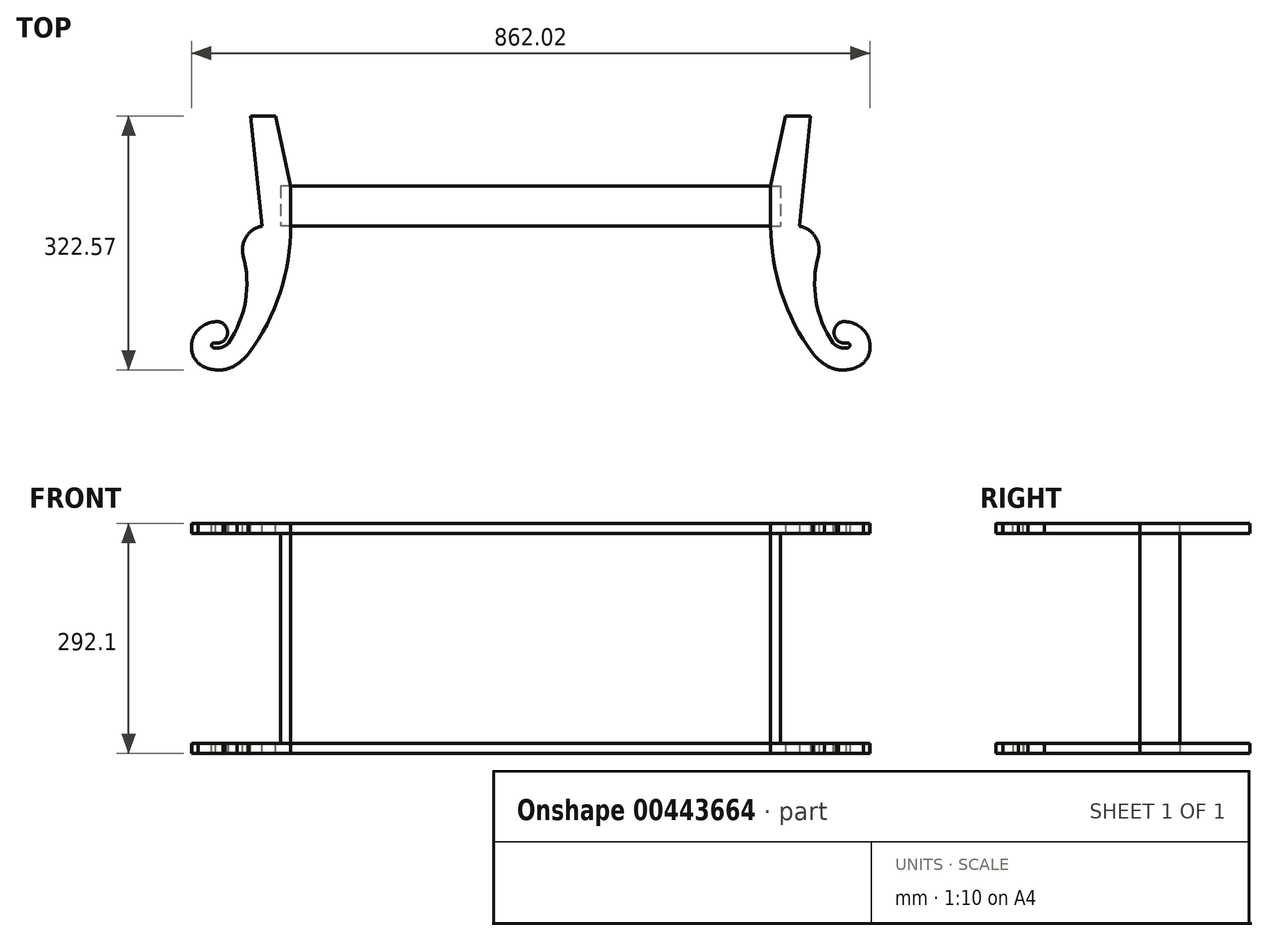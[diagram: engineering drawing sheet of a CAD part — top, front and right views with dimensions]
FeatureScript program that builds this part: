
annotation { "Feature Type Name" : "Feature", "Feature Type Description" : "" }
export const myFeature = defineFeature(function(context is Context, id is Id, definition is map)
    precondition{}
    {
        {
            var Q0;
            Q0=qCreatedBy(makeId("Front.planeOp"),FACE);
            var sketch = newSketch(context, id + "F0", { "sketchPlane" : qUnion([Q0])});
            skLineSegment(sketch, "E0.bottom", {"start": v(0, 0) * mm, "end": v(-609.6, 0) * mm});
            skLineSegment(sketch, "E0.top", {"start": v(0, 266.7) * mm, "end": v(-609.6, 266.7) * mm});
            skLineSegment(sketch, "E0.left", {"start": v(0, 0) * mm, "end": v(0, 266.7) * mm});
            skLineSegment(sketch, "E0.right", {"start": v(-609.6, 0) * mm, "end": v(-609.6, 266.7) * mm});
            skLineSegment(sketch, "E1.0", {"start": v(0, 279.4) * mm, "end": v(-609.6, 279.4) * mm});
            skLineSegment(sketch, "E1.1", {"start": v(12.7, 0) * mm, "end": v(12.7, 266.7) * mm});
            skLineSegment(sketch, "E1.2", {"start": v(0, -12.7) * mm, "end": v(-609.6, -12.7) * mm});
            skLineSegment(sketch, "E1.3", {"start": v(-622.3, 0) * mm, "end": v(-622.3, 266.7) * mm});
            skLineSegment(sketch, "E2", {"start": v(0, 266.7) * mm, "end": v(0, 279.4) * mm});
            skLineSegment(sketch, "E3", {"start": v(0, 266.7) * mm, "end": v(12.7, 266.7) * mm});
            skLineSegment(sketch, "E4", {"start": v(-609.6, 266.7) * mm, "end": v(-609.6, 279.4) * mm});
            skLineSegment(sketch, "E5", {"start": v(-609.6, 266.7) * mm, "end": v(-622.3, 266.7) * mm});
            skLineSegment(sketch, "E6", {"start": v(-609.6, 0) * mm, "end": v(-609.6, -12.7) * mm});
            skLineSegment(sketch, "E7", {"start": v(-609.6, 0) * mm, "end": v(-622.3, 0) * mm});
            skLineSegment(sketch, "E8", {"start": v(0, 0) * mm, "end": v(0, -12.7) * mm});
            skLineSegment(sketch, "E9", {"start": v(0, 0) * mm, "end": v(12.7, 0) * mm});
            skSolve(sketch);
        }
        {
            var Q0;
            Q0=makeQuery(id+"F0.imprint","IMPRINT",FACE,{"disambiguationData":[TD([[makeQuery(id+"F0.imprint","IMPRINT",EDGE,{"derivedFrom":sQuery(id+"F0.wireOp",EDGE,"E0.top")}),-1.0]])]});
            var Q1;
            Q1=makeQuery(id+"F0.imprint","IMPRINT",FACE,{"disambiguationData":[TD([[makeQuery(id+"F0.imprint","IMPRINT",EDGE,{"derivedFrom":sQuery(id+"F0.wireOp",EDGE,"E0.right")}),1.0]])]});
            var Q2;
            Q2=makeQuery(id+"F0.imprint","IMPRINT",FACE,{"disambiguationData":[TD([[makeQuery(id+"F0.imprint","IMPRINT",EDGE,{"derivedFrom":sQuery(id+"F0.wireOp",EDGE,"E0.bottom")}),1.0]])]});
            var Q3;
            Q3=makeQuery(id+"F0.imprint","IMPRINT",FACE,{"disambiguationData":[TD([[makeQuery(id+"F0.imprint","IMPRINT",EDGE,{"derivedFrom":sQuery(id+"F0.wireOp",EDGE,"E0.left")}),-1.0]])]});
            extrude(context, id + "F1", {"entities" : qUnion([Q0, Q1, Q2, Q3]), "oppositeDirection" : true, "depth" : 50.8 * mm});
        }
        {
            var Q0;
            Q0=makeQuery(id+"F1.opExtrude","SWEPT_FACE",FACE,{"disambiguationData":[OSD([sQuery(id+"F0.wireOp",EDGE,"E7")])]});
            var sketch = newSketch(context, id + "F2", { "sketchPlane" : qUnion([Q0])});
            skLineSegment(sketch, "E10", {"start": v(-660.4, -139.7) * mm, "end": v(-628.65, -139.7) * mm});
            skLineSegment(sketch, "E11", {"start": v(-609.6, -50.8) * mm, "end": v(-609.6, 0) * mm});
            skArc(sketch, "E12", {"start": v(-705.02, 121.4) * mm, "mid": v(-689.95, 135.71) * mm, "end": v(-706.36, 148.46) * mm});
            skArc(sketch, "E13", {"start": v(-688.65, 148.37) * mm, "mid": v(-697.3, 154.06) * mm, "end": v(-707.63, 154.68) * mm});
            skArc(sketch, "E14", {"start": v(-707.63, 154.68) * mm, "mid": v(-710.1, 150.94) * mm, "end": v(-706.36, 148.46) * mm});
            skArc(sketch, "E15", {"start": v(-609.6, 0) * mm, "mid": v(-623.28, 85.15) * mm, "end": v(-662.94, 161.73) * mm});
            skArc(sketch, "E16", {"start": v(-735.81, 154.3) * mm, "mid": v(-735.37, 148.14) * mm, "end": v(-733.92, 142.12) * mm});
            skPoint(sketch, "E17.start.orphan", {"position": v(-706.36, 182.77) * mm});
            skArc(sketch, "E18.trimOffspring", {"start": v(-733.92, 142.12) * mm, "mid": v(-722.3, 127.82) * mm, "end": v(-705.02, 121.4) * mm});
            skArc(sketch, "E19", {"start": v(-693.54, 182.23) * mm, "mid": v(-694.66, 182.44) * mm, "end": v(-695.78, 182.63) * mm});
            skArc(sketch, "E20", {"start": v(-695.78, 182.63) * mm, "mid": v(-704.55, 182.73) * mm, "end": v(-713.21, 181.36) * mm});
            skArc(sketch, "E21", {"start": v(-713.21, 181.36) * mm, "mid": v(-720.7, 178.48) * mm, "end": v(-727.26, 173.88) * mm});
            skArc(sketch, "E22", {"start": v(-727.26, 173.88) * mm, "mid": v(-733.45, 164.93) * mm, "end": v(-735.81, 154.3) * mm});
            skPoint(sketch, "E23.orphan", {"position": v(-691.05, 182.63) * mm});
            skArc(sketch, "E24", {"start": v(-662.94, 161.73) * mm, "mid": v(-669.92, 169.21) * mm, "end": v(-677.87, 175.63) * mm});
            skArc(sketch, "E25", {"start": v(-677.87, 175.63) * mm, "mid": v(-685.4, 179.67) * mm, "end": v(-693.54, 182.23) * mm});
            skLineSegment(sketch, "E26", {"start": v(-609.6, -50.8) * mm, "end": v(-628.65, -139.7) * mm});
            skPoint(sketch, "E27.orphan", {"position": v(-609.6, -139.7) * mm});
            skPoint(sketch, "E28.start.orphan", {"position": v(-673.1, -139.7) * mm});
            skLineSegment(sketch, "E29", {"start": v(-645.91, 0.13) * mm, "end": v(-660.4, -139.7) * mm});
            skPoint(sketch, "E30.orphan", {"position": v(-647.25, 0) * mm});
            skPoint(sketch, "E31.orphan", {"position": v(-736.6, -139.7) * mm});
            skArc(sketch, "E32", {"start": v(-670.05, 37.9) * mm, "mid": v(-666.34, 13.67) * mm, "end": v(-645.91, 0.13) * mm});
            skArc(sketch, "E33", {"start": v(-670.05, 37.9) * mm, "mid": v(-667.25, 95.17) * mm, "end": v(-688.65, 148.37) * mm});
            skSolve(sketch);
        }
        {
            var Q0;
            Q0=makeQuery(id+"F2.imprint","IMPRINT",FACE,{"disambiguationData":[TD([[makeQuery(id+"F2.imprint","IMPRINT",EDGE,{"derivedFrom":sQuery(id+"F2.wireOp",EDGE,"E10")}),1.0]])]});
            var Q1;
            Q1=makeQuery(id+"F2.imprint","IMPRINT",FACE,{"disambiguationData":[TD([[makeQuery(id+"F2.imprint","IMPRINT",EDGE,{"derivedFrom":sQuery(id+"F2.wireOp",EDGE,"E11")}),1.0]])]});
            extrude(context, id + "F3", {"entities" : qUnion([Q0, Q1]), "depth" : 12.7 * mm});
        }
        {
            var Q0;
            Q0=makeQuery(id+"F3.opExtrude","SWEPT_BODY",BODY,{"disambiguationData":[OSD([sQuery(id+"F2.wireOp",EDGE,"E10"),sQuery(id+"F2.wireOp",EDGE,"E11"),sQuery(id+"F2.wireOp",EDGE,"E12"),sQuery(id+"F2.wireOp",EDGE,"E13"),sQuery(id+"F2.wireOp",EDGE,"E14"),sQuery(id+"F2.wireOp",EDGE,"E15"),sQuery(id+"F2.wireOp",EDGE,"E16"),sQuery(id+"F2.wireOp",EDGE,"E18.trimOffspring"),sQuery(id+"F2.wireOp",EDGE,"E19"),sQuery(id+"F2.wireOp",EDGE,"E20"),sQuery(id+"F2.wireOp",EDGE,"E21"),sQuery(id+"F2.wireOp",EDGE,"E22"),sQuery(id+"F2.wireOp",EDGE,"E24"),sQuery(id+"F2.wireOp",EDGE,"E25"),sQuery(id+"F2.wireOp",EDGE,"E26"),sQuery(id+"F2.wireOp",EDGE,"E29"),sQuery(id+"F2.wireOp",EDGE,"jBR7SmMU-Rc7H-dq6u-iteg-TQdBeAZQFpAq")])]});
            transform(context, id + "F4", {"entities" : qUnion([Q0]), "transformType" : TransformType.TRANSLATION_3D, "dx" : 0 * mm, "dy" : 0 * mm, "dz" : 279.4 * mm, "makeCopy" : true});
        }
        {
            var Q0;
            Q0=makeQuery(id+"F3.opExtrude","SWEPT_BODY",BODY,{"disambiguationData":[OSD([sQuery(id+"F2.wireOp",EDGE,"E10"),sQuery(id+"F2.wireOp",EDGE,"E11"),sQuery(id+"F2.wireOp",EDGE,"E12"),sQuery(id+"F2.wireOp",EDGE,"E13"),sQuery(id+"F2.wireOp",EDGE,"E14"),sQuery(id+"F2.wireOp",EDGE,"E15"),sQuery(id+"F2.wireOp",EDGE,"E16"),sQuery(id+"F2.wireOp",EDGE,"E18.trimOffspring"),sQuery(id+"F2.wireOp",EDGE,"E19"),sQuery(id+"F2.wireOp",EDGE,"E20"),sQuery(id+"F2.wireOp",EDGE,"E21"),sQuery(id+"F2.wireOp",EDGE,"E22"),sQuery(id+"F2.wireOp",EDGE,"E24"),sQuery(id+"F2.wireOp",EDGE,"E25"),sQuery(id+"F2.wireOp",EDGE,"E26"),sQuery(id+"F2.wireOp",EDGE,"E29"),sQuery(id+"F2.wireOp",EDGE,"E32"),sQuery(id+"F2.wireOp",EDGE,"E33")])]});
            var Q1;
            Q1=makeQuery(id+"F1.opExtrude","SWEPT_EDGE",EDGE,{"disambiguationData":[OSD([sQuery(id+"F0.wireOp",EDGE,"E1.2"),sQuery(id+"F0.wireOp",EDGE,"E6")])]});
            transform(context, id + "F5", {"entities" : qUnion([Q0]), "transformType" : TransformType.ROTATION, "transformAxis" : qUnion([Q1]), "angle" : 180 * degree, "oppositeDirection" : true, "makeCopy" : true});
        }
        {
            var Q0;
            Q0=makeQuery(id+"F5.opPattern","COPY",BODY,{"derivedFrom":makeQuery(id+"F3.opExtrude","SWEPT_BODY",BODY,{"disambiguationData":[OSD([sQuery(id+"F2.wireOp",EDGE,"E10"),sQuery(id+"F2.wireOp",EDGE,"E11"),sQuery(id+"F2.wireOp",EDGE,"E12"),sQuery(id+"F2.wireOp",EDGE,"E13"),sQuery(id+"F2.wireOp",EDGE,"E14"),sQuery(id+"F2.wireOp",EDGE,"E15"),sQuery(id+"F2.wireOp",EDGE,"E16"),sQuery(id+"F2.wireOp",EDGE,"E18.trimOffspring"),sQuery(id+"F2.wireOp",EDGE,"E19"),sQuery(id+"F2.wireOp",EDGE,"E20"),sQuery(id+"F2.wireOp",EDGE,"E21"),sQuery(id+"F2.wireOp",EDGE,"E22"),sQuery(id+"F2.wireOp",EDGE,"E24"),sQuery(id+"F2.wireOp",EDGE,"E25"),sQuery(id+"F2.wireOp",EDGE,"E26"),sQuery(id+"F2.wireOp",EDGE,"E29"),sQuery(id+"F2.wireOp",EDGE,"E32"),sQuery(id+"F2.wireOp",EDGE,"E33")])]}),"instanceName":"1"});
            transform(context, id + "F6", {"entities" : qUnion([Q0]), "transformType" : TransformType.TRANSLATION_3D, "dx" : 609.6 * mm, "dy" : 0 * mm, "dz" : 12.7 * mm, "makeCopy" : true});
        }
        {
            var Q0;
            Q0=makeQuery(id+"F6.opPattern","COPY",BODY,{"derivedFrom":makeQuery(id+"F5.opPattern","COPY",BODY,{"derivedFrom":makeQuery(id+"F3.opExtrude","SWEPT_BODY",BODY,{"disambiguationData":[OSD([sQuery(id+"F2.wireOp",EDGE,"E10"),sQuery(id+"F2.wireOp",EDGE,"E11"),sQuery(id+"F2.wireOp",EDGE,"E12"),sQuery(id+"F2.wireOp",EDGE,"E13"),sQuery(id+"F2.wireOp",EDGE,"E14"),sQuery(id+"F2.wireOp",EDGE,"E15"),sQuery(id+"F2.wireOp",EDGE,"E16"),sQuery(id+"F2.wireOp",EDGE,"E18.trimOffspring"),sQuery(id+"F2.wireOp",EDGE,"E19"),sQuery(id+"F2.wireOp",EDGE,"E20"),sQuery(id+"F2.wireOp",EDGE,"E21"),sQuery(id+"F2.wireOp",EDGE,"E22"),sQuery(id+"F2.wireOp",EDGE,"E24"),sQuery(id+"F2.wireOp",EDGE,"E25"),sQuery(id+"F2.wireOp",EDGE,"E26"),sQuery(id+"F2.wireOp",EDGE,"E29"),sQuery(id+"F2.wireOp",EDGE,"E32"),sQuery(id+"F2.wireOp",EDGE,"E33")])]}),"instanceName":"1"}),"instanceName":"1"});
            transform(context, id + "F7", {"entities" : qUnion([Q0]), "transformType" : TransformType.TRANSLATION_3D, "dx" : 0 * mm, "dy" : 0 * mm, "dz" : 279.4 * mm, "makeCopy" : true});
        }
        {
            var Q0;
            Q0=makeQuery(id+"F5.opPattern","COPY",BODY,{"derivedFrom":makeQuery(id+"F3.opExtrude","SWEPT_BODY",BODY,{"disambiguationData":[OSD([sQuery(id+"F2.wireOp",EDGE,"E10"),sQuery(id+"F2.wireOp",EDGE,"E11"),sQuery(id+"F2.wireOp",EDGE,"E12"),sQuery(id+"F2.wireOp",EDGE,"E13"),sQuery(id+"F2.wireOp",EDGE,"E14"),sQuery(id+"F2.wireOp",EDGE,"E15"),sQuery(id+"F2.wireOp",EDGE,"E16"),sQuery(id+"F2.wireOp",EDGE,"E18.trimOffspring"),sQuery(id+"F2.wireOp",EDGE,"E19"),sQuery(id+"F2.wireOp",EDGE,"E20"),sQuery(id+"F2.wireOp",EDGE,"E21"),sQuery(id+"F2.wireOp",EDGE,"E22"),sQuery(id+"F2.wireOp",EDGE,"E24"),sQuery(id+"F2.wireOp",EDGE,"E25"),sQuery(id+"F2.wireOp",EDGE,"E26"),sQuery(id+"F2.wireOp",EDGE,"E29"),sQuery(id+"F2.wireOp",EDGE,"E32"),sQuery(id+"F2.wireOp",EDGE,"E33")])]}),"instanceName":"1"});
            deleteBodies(context, id + "F8", {"entities" : qUnion([Q0])});
        }
        {
            var Q0;
            {var subQ0=sQuery(id+"F0.wireOp",EDGE,"E0.top");var subQ1=sQuery(id+"F0.wireOp",EDGE,"E4");Q0=makeQuery(id+"F1.opExtrude","CAP_VERTEX",VERTEX,{"disambiguationData":[OSD([subQ0,sQuery(id+"F0.wireOp",EDGE,"E0.right"),subQ1,sQuery(id+"F0.wireOp",EDGE,"E5")]),topologyDisambiguationEdgeConnected([makeQuery(id+"F0.imprint","IMPRINT",EDGE,{"derivedFrom":subQ0})])],"isStart":true});}
            var Q1;
            Q1=makeQuery(id+"F4.opPattern","COPY",VERTEX,{"derivedFrom":makeQuery(id+"F3.opExtrude","CAP_VERTEX",VERTEX,{"disambiguationData":[OSD([sQuery(id+"F2.wireOp",EDGE,"E15"),sQuery(id+"F2.wireOp",EDGE,"E24")])],"isStart":false}),"instanceName":"1"});
            var Q2;
            {var subQ0=sQuery(id+"F0.wireOp",EDGE,"E0.bottom");var subQ1=sQuery(id+"F0.wireOp",EDGE,"E6");Q2=makeQuery(id+"F1.opExtrude","CAP_VERTEX",VERTEX,{"disambiguationData":[OSD([subQ0,sQuery(id+"F0.wireOp",EDGE,"E0.right"),subQ1,sQuery(id+"F0.wireOp",EDGE,"E7")]),topologyDisambiguationEdgeConnected([makeQuery(id+"F0.imprint","IMPRINT",EDGE,{"derivedFrom":subQ0})])],"isStart":true});}
            cPlane(context, id + "F9", {"entities" : qUnion([Q0, Q1, Q2]), "cplaneType" : CPlaneType.THREE_POINT, "offset" : 25.4 * mm, "width" : 152.4 * mm, "height" : 152.4 * mm});
        }
    });
